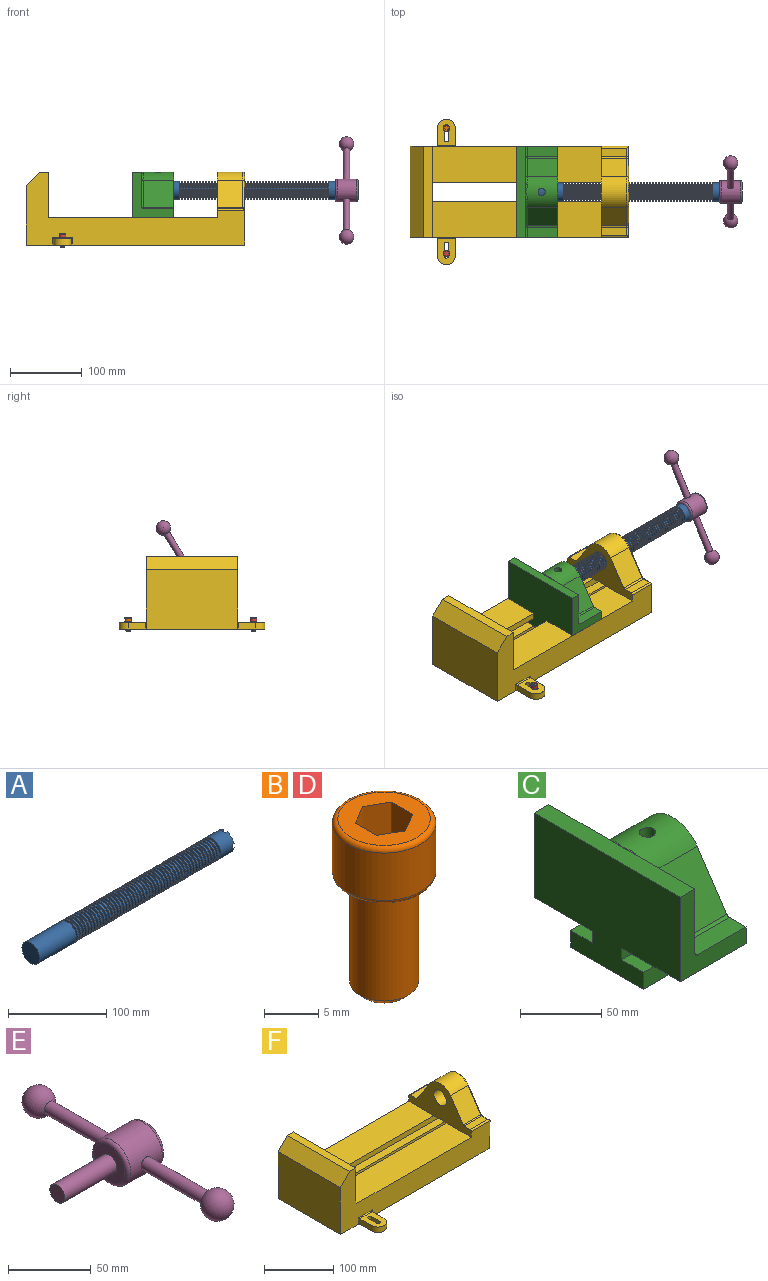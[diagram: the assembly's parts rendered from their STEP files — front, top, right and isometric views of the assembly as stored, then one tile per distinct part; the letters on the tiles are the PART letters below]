
ASSEMBLY  parts=6 mates=6
PART A: 220 faces, bbox 279.4x25.4x25.4 mm
  f0: cylinder r=12.7mm len=25.4mm, axis (-1,0,0), area 1468.2mm2, adj f1,f2,f3,f5,f7,f208,f209,f210
  f1: plane 9.9x9.9mm, normal (1,0,0), area 62.3mm2, adj f0,f4,f213,f216
  f2: plane 9.9x9.9mm, normal (1,0,0), area 62.3mm2, adj f0,f4,f210,f218
  f3: plane 9.9x9.9mm, normal (1,0,0), area 62.3mm2, adj f0,f4,f209,f212
  f4: cylinder r=6.35mm len=25.4mm, axis (1,0,0), area 960.3mm2, adj f1,f2,f3,f5,f6,f208,f209,f210
  f5: plane 9.9x9.9mm, normal (1,0,0), area 62.3mm2, adj f0,f4,f215,f217
  f6: plane 12.7x12.7mm, normal (1,0,0), area 126.7mm2, adj f4
  f7: cone r=12.7mm half-angle=76deg, axis (1,0,0), area 188mm2, adj f0,f9
  f8: cone r=10.16mm half-angle=76deg, axis (-1,0,0), area 188mm2, adj f9,f10
  f9: cylinder r=10.16mm len=20.32mm, axis (1,0,0), area 81.1mm2, adj f7,f8
  f10: cylinder r=12.7mm len=25.4mm, axis (-1,0,0), area 131.7mm2, adj f8,f11
  f11: cone r=12.7mm half-angle=76deg, axis (1,0,0), area 188mm2, adj f10,f13
  f12: cone r=10.16mm half-angle=76deg, axis (-1,0,0), area 188mm2, adj f13,f14
  f13: cylinder r=10.16mm len=20.32mm, axis (1,0,0), area 81.1mm2, adj f11,f12
  f14: cylinder r=12.7mm len=25.4mm, axis (-1,0,0), area 131.7mm2, adj f12,f15
  f15: cone r=12.7mm half-angle=76deg, axis (1,0,0), area 188mm2, adj f14,f17
  f16: cone r=10.16mm half-angle=76deg, axis (-1,0,0), area 188mm2, adj f17,f18
  f17: cylinder r=10.16mm len=20.32mm, axis (1,0,0), area 81.1mm2, adj f15,f16
  f18: cylinder r=12.7mm len=25.4mm, axis (-1,0,0), area 131.7mm2, adj f16,f19
  f19: cone r=12.7mm half-angle=76deg, axis (1,0,0), area 188mm2, adj f18,f21
  f20: cone r=10.16mm half-angle=76deg, axis (-1,0,0), area 188mm2, adj f21,f22
  f21: cylinder r=10.16mm len=20.32mm, axis (1,0,0), area 81.1mm2, adj f19,f20
  f22: cylinder r=12.7mm len=25.4mm, axis (-1,0,0), area 131.7mm2, adj f20,f23
  f23: cone r=12.7mm half-angle=76deg, axis (1,0,0), area 188mm2, adj f22,f25
  f24: cone r=10.16mm half-angle=76deg, axis (-1,0,0), area 188mm2, adj f25,f26
  f25: cylinder r=10.16mm len=20.32mm, axis (1,0,0), area 81.1mm2, adj f23,f24
  f26: cylinder r=12.7mm len=25.4mm, axis (-1,0,0), area 131.7mm2, adj f24,f27
  f27: cone r=12.7mm half-angle=76deg, axis (1,0,0), area 188mm2, adj f26,f29
  f28: cone r=10.16mm half-angle=76deg, axis (-1,0,0), area 188mm2, adj f29,f30
  f29: cylinder r=10.16mm len=20.32mm, axis (1,0,0), area 81.1mm2, adj f27,f28
  f30: cylinder r=12.7mm len=25.4mm, axis (-1,0,0), area 131.7mm2, adj f28,f31
  f31: cone r=12.7mm half-angle=76deg, axis (1,0,0), area 188mm2, adj f30,f33
  f32: cone r=10.16mm half-angle=76deg, axis (-1,0,0), area 188mm2, adj f33,f34
  f33: cylinder r=10.16mm len=20.32mm, axis (1,0,0), area 81.1mm2, adj f31,f32
  f34: cylinder r=12.7mm len=25.4mm, axis (-1,0,0), area 131.7mm2, adj f32,f35
  f35: cone r=12.7mm half-angle=76deg, axis (1,0,0), area 188mm2, adj f34,f37
  f36: cone r=10.16mm half-angle=76deg, axis (-1,0,0), area 188mm2, adj f37,f38
  f37: cylinder r=10.16mm len=20.32mm, axis (1,0,0), area 81.1mm2, adj f35,f36
  f38: cylinder r=12.7mm len=25.4mm, axis (-1,0,0), area 131.7mm2, adj f36,f39
  f39: cone r=12.7mm half-angle=76deg, axis (1,0,0), area 188mm2, adj f38,f41
  f40: cone r=10.16mm half-angle=76deg, axis (-1,0,0), area 188mm2, adj f41,f42
  f41: cylinder r=10.16mm len=20.32mm, axis (1,0,0), area 81.1mm2, adj f39,f40
  f42: cylinder r=12.7mm len=25.4mm, axis (-1,0,0), area 131.7mm2, adj f40,f43
  f43: cone r=12.7mm half-angle=76deg, axis (1,0,0), area 188mm2, adj f42,f45
  f44: cone r=10.16mm half-angle=76deg, axis (-1,0,0), area 188mm2, adj f45,f46
  f45: cylinder r=10.16mm len=20.32mm, axis (1,0,0), area 81.1mm2, adj f43,f44
  f46: cylinder r=12.7mm len=25.4mm, axis (-1,0,0), area 131.7mm2, adj f44,f47
  f47: cone r=12.7mm half-angle=76deg, axis (1,0,0), area 188mm2, adj f46,f49
  f48: cone r=10.16mm half-angle=76deg, axis (-1,0,0), area 188mm2, adj f49,f50
  f49: cylinder r=10.16mm len=20.32mm, axis (1,0,0), area 81.1mm2, adj f47,f48
  f50: cylinder r=12.7mm len=25.4mm, axis (-1,0,0), area 131.7mm2, adj f48,f51
  f51: cone r=12.7mm half-angle=76deg, axis (1,0,0), area 188mm2, adj f50,f53
  f52: cone r=10.16mm half-angle=76deg, axis (-1,0,0), area 188mm2, adj f53,f54
  f53: cylinder r=10.16mm len=20.32mm, axis (1,0,0), area 81.1mm2, adj f51,f52
  f54: cylinder r=12.7mm len=25.4mm, axis (-1,0,0), area 131.7mm2, adj f52,f55
  f55: cone r=12.7mm half-angle=76deg, axis (1,0,0), area 188mm2, adj f54,f57
  f56: cone r=10.16mm half-angle=76deg, axis (-1,0,0), area 188mm2, adj f57,f58
  f57: cylinder r=10.16mm len=20.32mm, axis (1,0,0), area 81.1mm2, adj f55,f56
  f58: cylinder r=12.7mm len=25.4mm, axis (-1,0,0), area 131.7mm2, adj f56,f59
  f59: cone r=12.7mm half-angle=76deg, axis (1,0,0), area 188mm2, adj f58,f61
  f60: cone r=10.16mm half-angle=76deg, axis (-1,0,0), area 188mm2, adj f61,f62
  f61: cylinder r=10.16mm len=20.32mm, axis (1,0,0), area 81.1mm2, adj f59,f60
  f62: cylinder r=12.7mm len=25.4mm, axis (-1,0,0), area 131.7mm2, adj f60,f63
  f63: cone r=12.7mm half-angle=76deg, axis (1,0,0), area 188mm2, adj f62,f65
  f64: cone r=10.16mm half-angle=76deg, axis (-1,0,0), area 188mm2, adj f65,f66
  f65: cylinder r=10.16mm len=20.32mm, axis (1,0,0), area 81.1mm2, adj f63,f64
  f66: cylinder r=12.7mm len=25.4mm, axis (-1,0,0), area 131.7mm2, adj f64,f67
  f67: cone r=12.7mm half-angle=76deg, axis (1,0,0), area 188mm2, adj f66,f69
  f68: cone r=10.16mm half-angle=76deg, axis (-1,0,0), area 188mm2, adj f69,f70
  f69: cylinder r=10.16mm len=20.32mm, axis (1,0,0), area 81.1mm2, adj f67,f68
  f70: cylinder r=12.7mm len=25.4mm, axis (-1,0,0), area 131.7mm2, adj f68,f71
  f71: cone r=12.7mm half-angle=76deg, axis (1,0,0), area 188mm2, adj f70,f73
  f72: cone r=10.16mm half-angle=76deg, axis (-1,0,0), area 188mm2, adj f73,f74
  f73: cylinder r=10.16mm len=20.32mm, axis (1,0,0), area 81.1mm2, adj f71,f72
  f74: cylinder r=12.7mm len=25.4mm, axis (-1,0,0), area 131.7mm2, adj f72,f75
  f75: cone r=12.7mm half-angle=76deg, axis (1,0,0), area 188mm2, adj f74,f77
  f76: cone r=10.16mm half-angle=76deg, axis (-1,0,0), area 188mm2, adj f77,f78
  f77: cylinder r=10.16mm len=20.32mm, axis (1,0,0), area 81.1mm2, adj f75,f76
  f78: cylinder r=12.7mm len=25.4mm, axis (-1,0,0), area 131.7mm2, adj f76,f79
  f79: cone r=12.7mm half-angle=76deg, axis (1,0,0), area 188mm2, adj f78,f81
  f80: cone r=10.16mm half-angle=76deg, axis (-1,0,0), area 188mm2, adj f81,f82
  f81: cylinder r=10.16mm len=20.32mm, axis (1,0,0), area 81.1mm2, adj f79,f80
  f82: cylinder r=12.7mm len=25.4mm, axis (-1,0,0), area 131.7mm2, adj f80,f83
  f83: cone r=12.7mm half-angle=76deg, axis (1,0,0), area 188mm2, adj f82,f85
  f84: cone r=10.16mm half-angle=76deg, axis (-1,0,0), area 188mm2, adj f85,f86
  f85: cylinder r=10.16mm len=20.32mm, axis (1,0,0), area 81.1mm2, adj f83,f84
  f86: cylinder r=12.7mm len=25.4mm, axis (-1,0,0), area 131.7mm2, adj f84,f87
  f87: cone r=12.7mm half-angle=76deg, axis (1,0,0), area 188mm2, adj f86,f89
  f88: cone r=10.16mm half-angle=76deg, axis (-1,0,0), area 188mm2, adj f89,f90
  f89: cylinder r=10.16mm len=20.32mm, axis (1,0,0), area 81.1mm2, adj f87,f88
  f90: cylinder r=12.7mm len=25.4mm, axis (-1,0,0), area 131.7mm2, adj f88,f91
  f91: cone r=12.7mm half-angle=76deg, axis (1,0,0), area 188mm2, adj f90,f93
  f92: cone r=10.16mm half-angle=76deg, axis (-1,0,0), area 188mm2, adj f93,f94
  f93: cylinder r=10.16mm len=20.32mm, axis (1,0,0), area 81.1mm2, adj f91,f92
  f94: cylinder r=12.7mm len=25.4mm, axis (-1,0,0), area 131.7mm2, adj f92,f95
  f95: cone r=12.7mm half-angle=76deg, axis (1,0,0), area 188mm2, adj f94,f97
  f96: cone r=10.16mm half-angle=76deg, axis (-1,0,0), area 188mm2, adj f97,f98
  f97: cylinder r=10.16mm len=20.32mm, axis (1,0,0), area 81.1mm2, adj f95,f96
  f98: cylinder r=12.7mm len=25.4mm, axis (-1,0,0), area 131.7mm2, adj f96,f99
  f99: cone r=12.7mm half-angle=76deg, axis (1,0,0), area 188mm2, adj f98,f101
  f100: cone r=10.16mm half-angle=76deg, axis (-1,0,0), area 188mm2, adj f101,f102
  f101: cylinder r=10.16mm len=20.32mm, axis (1,0,0), area 81.1mm2, adj f99,f100
  f102: cylinder r=12.7mm len=25.4mm, axis (-1,0,0), area 131.7mm2, adj f100,f103
  f103: cone r=12.7mm half-angle=76deg, axis (1,0,0), area 188mm2, adj f102,f105
  f104: cone r=10.16mm half-angle=76deg, axis (-1,0,0), area 188mm2, adj f105,f106
  f105: cylinder r=10.16mm len=20.32mm, axis (1,0,0), area 81.1mm2, adj f103,f104
  f106: cylinder r=12.7mm len=25.4mm, axis (-1,0,0), area 131.7mm2, adj f104,f107
  f107: cone r=12.7mm half-angle=76deg, axis (1,0,0), area 188mm2, adj f106,f109
  f108: cone r=10.16mm half-angle=76deg, axis (-1,0,0), area 188mm2, adj f109,f110
  f109: cylinder r=10.16mm len=20.32mm, axis (1,0,0), area 81.1mm2, adj f107,f108
  f110: cylinder r=12.7mm len=25.4mm, axis (-1,0,0), area 131.7mm2, adj f108,f111
  f111: cone r=12.7mm half-angle=76deg, axis (1,0,0), area 188mm2, adj f110,f113
  f112: cone r=10.16mm half-angle=76deg, axis (-1,0,0), area 188mm2, adj f113,f114
  f113: cylinder r=10.16mm len=20.32mm, axis (1,0,0), area 81.1mm2, adj f111,f112
  f114: cylinder r=12.7mm len=25.4mm, axis (-1,0,0), area 131.7mm2, adj f112,f115
  f115: cone r=12.7mm half-angle=76deg, axis (1,0,0), area 188mm2, adj f114,f117
  f116: cone r=10.16mm half-angle=76deg, axis (-1,0,0), area 188mm2, adj f117,f118
  f117: cylinder r=10.16mm len=20.32mm, axis (1,0,0), area 81.1mm2, adj f115,f116
  f118: cylinder r=12.7mm len=25.4mm, axis (-1,0,0), area 131.7mm2, adj f116,f119
  f119: cone r=12.7mm half-angle=76deg, axis (1,0,0), area 188mm2, adj f118,f121
  f120: cone r=10.16mm half-angle=76deg, axis (-1,0,0), area 188mm2, adj f121,f122
  f121: cylinder r=10.16mm len=20.32mm, axis (1,0,0), area 81.1mm2, adj f119,f120
  f122: cylinder r=12.7mm len=25.4mm, axis (-1,0,0), area 131.7mm2, adj f120,f123
  f123: cone r=12.7mm half-angle=76deg, axis (1,0,0), area 188mm2, adj f122,f125
  f124: cone r=10.16mm half-angle=76deg, axis (-1,0,0), area 188mm2, adj f125,f126
  f125: cylinder r=10.16mm len=20.32mm, axis (1,0,0), area 81.1mm2, adj f123,f124
  f126: cylinder r=12.7mm len=25.4mm, axis (-1,0,0), area 131.7mm2, adj f124,f127
  f127: cone r=12.7mm half-angle=76deg, axis (1,0,0), area 188mm2, adj f126,f129
  f128: cone r=10.16mm half-angle=76deg, axis (-1,0,0), area 188mm2, adj f129,f130
  f129: cylinder r=10.16mm len=20.32mm, axis (1,0,0), area 81.1mm2, adj f127,f128
  f130: cylinder r=12.7mm len=25.4mm, axis (-1,0,0), area 131.7mm2, adj f128,f131
  f131: cone r=12.7mm half-angle=76deg, axis (1,0,0), area 188mm2, adj f130,f133
  f132: cone r=10.16mm half-angle=76deg, axis (-1,0,0), area 188mm2, adj f133,f134
  f133: cylinder r=10.16mm len=20.32mm, axis (1,0,0), area 81.1mm2, adj f131,f132
  f134: cylinder r=12.7mm len=25.4mm, axis (-1,0,0), area 131.7mm2, adj f132,f135
  f135: cone r=12.7mm half-angle=76deg, axis (1,0,0), area 188mm2, adj f134,f137
  f136: cone r=10.16mm half-angle=76deg, axis (-1,0,0), area 188mm2, adj f137,f138
  f137: cylinder r=10.16mm len=20.32mm, axis (1,0,0), area 81.1mm2, adj f135,f136
  f138: cylinder r=12.7mm len=25.4mm, axis (-1,0,0), area 131.7mm2, adj f136,f139
  f139: cone r=12.7mm half-angle=76deg, axis (1,0,0), area 188mm2, adj f138,f141
  f140: cone r=10.16mm half-angle=76deg, axis (-1,0,0), area 188mm2, adj f141,f142
  f141: cylinder r=10.16mm len=20.32mm, axis (1,0,0), area 81.1mm2, adj f139,f140
  f142: cylinder r=12.7mm len=25.4mm, axis (-1,0,0), area 131.7mm2, adj f140,f143
  f143: cone r=12.7mm half-angle=76deg, axis (1,0,0), area 188mm2, adj f142,f145
  f144: cone r=10.16mm half-angle=76deg, axis (-1,0,0), area 188mm2, adj f145,f146
  f145: cylinder r=10.16mm len=20.32mm, axis (1,0,0), area 81.1mm2, adj f143,f144
  f146: cylinder r=12.7mm len=25.4mm, axis (-1,0,0), area 131.7mm2, adj f144,f147
  f147: cone r=12.7mm half-angle=76deg, axis (1,0,0), area 188mm2, adj f146,f149
  f148: cone r=10.16mm half-angle=76deg, axis (-1,0,0), area 188mm2, adj f149,f150
  f149: cylinder r=10.16mm len=20.32mm, axis (1,0,0), area 81.1mm2, adj f147,f148
  f150: cylinder r=12.7mm len=25.4mm, axis (-1,0,0), area 131.7mm2, adj f148,f151
  f151: cone r=12.7mm half-angle=76deg, axis (1,0,0), area 188mm2, adj f150,f153
  f152: cone r=10.16mm half-angle=76deg, axis (-1,0,0), area 188mm2, adj f153,f154
  f153: cylinder r=10.16mm len=20.32mm, axis (1,0,0), area 81.1mm2, adj f151,f152
  f154: cylinder r=12.7mm len=25.4mm, axis (-1,0,0), area 131.7mm2, adj f152,f155
  f155: cone r=12.7mm half-angle=76deg, axis (1,0,0), area 188mm2, adj f154,f157
  f156: cone r=10.16mm half-angle=76deg, axis (-1,0,0), area 188mm2, adj f157,f158
  f157: cylinder r=10.16mm len=20.32mm, axis (1,0,0), area 81.1mm2, adj f155,f156
  f158: cylinder r=12.7mm len=25.4mm, axis (-1,0,0), area 131.7mm2, adj f156,f159
  f159: cone r=12.7mm half-angle=76deg, axis (1,0,0), area 188mm2, adj f158,f161
  f160: cone r=10.16mm half-angle=76deg, axis (-1,0,0), area 188mm2, adj f161,f162
  f161: cylinder r=10.16mm len=20.32mm, axis (1,0,0), area 81.1mm2, adj f159,f160
  f162: cylinder r=12.7mm len=25.4mm, axis (-1,0,0), area 131.7mm2, adj f160,f163
  f163: cone r=12.7mm half-angle=76deg, axis (1,0,0), area 188mm2, adj f162,f165
  f164: cone r=10.16mm half-angle=76deg, axis (-1,0,0), area 188mm2, adj f165,f166
  f165: cylinder r=10.16mm len=20.32mm, axis (1,0,0), area 81.1mm2, adj f163,f164
  f166: cylinder r=12.7mm len=25.4mm, axis (-1,0,0), area 131.7mm2, adj f164,f167
  f167: cone r=12.7mm half-angle=76deg, axis (1,0,0), area 188mm2, adj f166,f169
  f168: cone r=10.16mm half-angle=76deg, axis (-1,0,0), area 188mm2, adj f169,f170
  f169: cylinder r=10.16mm len=20.32mm, axis (1,0,0), area 81.1mm2, adj f167,f168
  f170: cylinder r=12.7mm len=25.4mm, axis (-1,0,0), area 131.7mm2, adj f168,f171
  f171: cone r=12.7mm half-angle=76deg, axis (1,0,0), area 188mm2, adj f170,f173
  f172: cone r=10.16mm half-angle=76deg, axis (-1,0,0), area 188mm2, adj f173,f174
  f173: cylinder r=10.16mm len=20.32mm, axis (1,0,0), area 81.1mm2, adj f171,f172
  f174: cylinder r=12.7mm len=25.4mm, axis (-1,0,0), area 131.7mm2, adj f172,f175
  f175: cone r=12.7mm half-angle=76deg, axis (1,0,0), area 188mm2, adj f174,f177
  f176: cone r=10.16mm half-angle=76deg, axis (-1,0,0), area 188mm2, adj f177,f178
  f177: cylinder r=10.16mm len=20.32mm, axis (1,0,0), area 81.1mm2, adj f175,f176
  f178: cylinder r=12.7mm len=25.4mm, axis (-1,0,0), area 131.7mm2, adj f176,f179
  f179: cone r=12.7mm half-angle=76deg, axis (1,0,0), area 188mm2, adj f178,f181
  f180: cone r=10.16mm half-angle=76deg, axis (-1,0,0), area 188mm2, adj f181,f182
  f181: cylinder r=10.16mm len=20.32mm, axis (1,0,0), area 81.1mm2, adj f179,f180
  f182: cylinder r=12.7mm len=25.4mm, axis (-1,0,0), area 131.7mm2, adj f180,f183
  f183: cone r=12.7mm half-angle=76deg, axis (1,0,0), area 188mm2, adj f182,f185
  f184: cone r=10.16mm half-angle=76deg, axis (-1,0,0), area 188mm2, adj f185,f186
  f185: cylinder r=10.16mm len=20.32mm, axis (1,0,0), area 81.1mm2, adj f183,f184
  f186: cylinder r=12.7mm len=25.4mm, axis (-1,0,0), area 131.7mm2, adj f184,f187
  f187: cone r=12.7mm half-angle=76deg, axis (1,0,0), area 188mm2, adj f186,f189
  f188: cone r=10.16mm half-angle=76deg, axis (-1,0,0), area 188mm2, adj f189,f190
  f189: cylinder r=10.16mm len=20.32mm, axis (1,0,0), area 81.1mm2, adj f187,f188
  f190: cylinder r=12.7mm len=25.4mm, axis (-1,0,0), area 131.7mm2, adj f188,f191
  f191: cone r=12.7mm half-angle=76deg, axis (1,0,0), area 188mm2, adj f190,f193
  f192: cone r=10.16mm half-angle=76deg, axis (-1,0,0), area 188mm2, adj f193,f194
  f193: cylinder r=10.16mm len=20.32mm, axis (1,0,0), area 81.1mm2, adj f191,f192
  f194: cylinder r=12.7mm len=25.4mm, axis (-1,0,0), area 131.7mm2, adj f192,f195
  f195: cone r=12.7mm half-angle=76deg, axis (1,0,0), area 188mm2, adj f194,f197
  f196: cone r=10.16mm half-angle=76deg, axis (-1,0,0), area 188mm2, adj f197,f198
  f197: cylinder r=10.16mm len=20.32mm, axis (1,0,0), area 81.1mm2, adj f195,f196
  f198: cylinder r=12.7mm len=25.4mm, axis (-1,0,0), area 131.7mm2, adj f196,f199
  f199: cone r=12.7mm half-angle=76deg, axis (1,0,0), area 188mm2, adj f198,f201
  f200: cone r=10.16mm half-angle=76deg, axis (-1,0,0), area 188mm2, adj f201,f202
  f201: cylinder r=10.16mm len=20.32mm, axis (1,0,0), area 81.1mm2, adj f199,f200
  f202: cylinder r=12.7mm len=25.4mm, axis (-1,0,0), area 131.7mm2, adj f200,f203
  f203: cone r=12.7mm half-angle=76deg, axis (1,0,0), area 188mm2, adj f202,f205
  f204: cone r=10.16mm half-angle=76deg, axis (-1,0,0), area 188mm2, adj f205,f207
  f205: cylinder r=10.16mm len=20.32mm, axis (1,0,0), area 81.1mm2, adj f203,f204
  f206: plane 25.4x25.4mm, normal (-1,0,0), area 506.7mm2, adj f207
  f207: cylinder r=12.7mm len=52.45mm, axis (-1,0,0), area 4185.4mm2, adj f204,f206
  f208: plane 6.88x5.08mm, normal (1,0,0), area 32.7mm2, adj f0,f4,f209,f210
  f209: plane 6.62x2.54mm, normal (0,-1,0), area 16.8mm2, adj f0,f3,f4,f208
  f210: plane 6.62x2.54mm, normal (0,1,0), area 16.8mm2, adj f0,f2,f4,f208
  f211: plane 6.88x5.08mm, normal (1,0,0), area 32.7mm2, adj f0,f4,f212,f213
  f212: plane 6.62x2.54mm, normal (0,0,1), area 16.8mm2, adj f0,f3,f4,f211
  f213: plane 6.62x2.54mm, normal (0,0,-1), area 16.8mm2, adj f0,f1,f4,f211
  f214: plane 6.88x5.08mm, normal (1,0,0), area 32.7mm2, adj f0,f4,f215,f216
  f215: plane 6.62x2.54mm, normal (0,1,0), area 16.8mm2, adj f0,f4,f5,f214
  f216: plane 6.62x2.54mm, normal (0,-1,0), area 16.8mm2, adj f0,f1,f4,f214
  f217: plane 6.62x2.54mm, normal (0,0,-1), area 16.8mm2, adj f0,f4,f5,f219
  f218: plane 6.62x2.54mm, normal (0,0,1), area 16.8mm2, adj f0,f2,f4,f219
  f219: plane 6.88x5.08mm, normal (1,0,0), area 32.7mm2, adj f0,f4,f217,f218
PART B: 15 faces, bbox 10.3x10.3x19.1 mm
  f0: plane 8.51x8.51mm, normal (0,0,1), area 37.2mm2, adj f5,f6,f7,f8,f9,f10,f14
  f1: cylinder r=3.17mm len=11.94mm, axis (0,0,1), area 238.2mm2, adj f4,f12
  f2: plane 4.83x4.83mm, normal (0,0,-1), area 18.3mm2, adj f12
  f3: cylinder r=4.76mm len=9.53mm, axis (0,0,-1), area 159.6mm2, adj f13,f14
  f4: plane 8.51x8.51mm, normal (0,0,-1), area 25.2mm2, adj f1,f13
  f5: plane 4.83x2.38mm, normal (-0.5,-0.87,0), area 13.3mm2, adj f0,f6,f10,f11
  f6: plane 4.83x2.38mm, normal (0.5,-0.87,0), area 13.3mm2, adj f0,f5,f7,f11
  f7: plane 4.83x2.75mm, normal (1,0,0), area 13.3mm2, adj f0,f6,f8,f11
  f8: plane 4.83x2.38mm, normal (0.5,0.87,0), area 13.3mm2, adj f0,f7,f9,f11
  f9: plane 4.83x2.38mm, normal (-0.5,0.87,0), area 13.3mm2, adj f0,f8,f10,f11
  f10: plane 4.83x2.75mm, normal (-1,0,0), area 13.3mm2, adj f0,f5,f9,f11
  f11: plane 5.5x4.76mm, normal (0,0,1), area 19.6mm2, adj f5,f6,f7,f8,f9,f10
  f12: cone r=3.17mm half-angle=45deg, axis (0,0,1), area 18.9mm2, adj f1,f2
  f13: torus R=4.25mm, axis (0,0,1), area 23mm2, adj f3,f4
  f14: torus R=4.25mm, axis (0,0,1), area 23mm2, adj f0,f3
PART C: 36 faces, bbox 57.2x127x89 mm
  f0: plane 57.15x50.8mm, normal (0,0,-1), area 2903.2mm2, adj f6,f9,f10,f23
  f1: cylinder r=12.7mm len=44.45mm, axis (1,0,0), area 3464.3mm2, adj f6,f15,f16
  f2: plane 41.91x14.52mm, normal (0,0,1), area 608.5mm2, adj f6,f11,f24,f25
  f3: plane 51.86x48.26mm, normal (1,0,0), area 1495.7mm2, adj f8,f10,f31,f33,f35
  f4: plane 51.86x48.26mm, normal (1,0,0), area 1495.7mm2, adj f8,f11,f24,f28,f29
  f5: plane 57.15x50.8mm, normal (0,0,-1), area 2903.2mm2, adj f6,f9,f11,f22
  f6: plane 127x85.09mm, normal (1,0,0), area 5190.6mm2, adj f0,f1,f2,f5,f7,f10,f11,f12
  f7: plane 41.91x14.52mm, normal (0,0,1), area 608.5mm2, adj f6,f10,f30,f31
  f8: plane 127x12.7mm, normal (0,0,1), area 1612.9mm2, adj f3,f4,f9,f10,f11,f26,f34
  f9: plane 127x85.09mm, normal (-1,0,0), area 9096.8mm2, adj f0,f5,f8,f10,f11,f17,f18,f19
  f10: plane 63.5x57.15mm, normal (0,-1,0), area 1372.3mm2, adj f0,f3,f6,f7,f8,f9,f31
  f11: plane 63.5x57.15mm, normal (0,1,0), area 1372.3mm2, adj f2,f4,f5,f6,f8,f9,f24
  f12: plane 41.91x38.43mm, normal (0,-0.83,0.56), area 1939.2mm2, adj f6,f13,f30,f33
  f13: cylinder r=25.4mm len=44.45mm, axis (1,0,0), area 2026.5mm2, adj f6,f12,f14,f16,f26,f28,f34,f35
  f14: plane 41.91x38.43mm, normal (0,0.83,0.56), area 1939.2mm2, adj f6,f13,f25,f29
  f15: plane 25.4x25.4mm, normal (1,0,0), area 506.7mm2, adj f1
  f16: cylinder r=5.08mm len=13.76mm, axis (0,0,1), area 414mm2, adj f1,f13
  f17: plane 57.15x19.05mm, normal (0,0,1), area 1088.7mm2, adj f6,f9,f18,f23
  f18: plane 57.15x12.7mm, normal (0,-1,0), area 725.8mm2, adj f6,f9,f17,f19
  f19: plane 63.5x57.15mm, normal (0,0,-1), area 3629mm2, adj f6,f9,f18,f20
  f20: plane 57.15x12.7mm, normal (0,1,0), area 725.8mm2, adj f6,f9,f19,f21
  f21: plane 57.15x19.05mm, normal (0,0,1), area 1088.7mm2, adj f6,f9,f20,f22
  f22: plane 57.15x8.89mm, normal (0,1,0), area 508.1mm2, adj f5,f6,f9,f21
  f23: plane 57.15x8.89mm, normal (0,-1,0), area 508.1mm2, adj f0,f6,f9,f17
  f24: cylinder r=2.54mm len=14.52mm, axis (0,-1,0), area 57.9mm2, adj f2,f4,f11,f27
  f25: cylinder r=2.54mm len=41.91mm, axis (1,0,0), area 104.3mm2, adj f2,f6,f14,f27
  f26: bspline ~12.24x2.8mm, area 20.9mm2, adj f8,f13,f28
  f27: sphere r=2.54mm, area 6.3mm2, adj f24,f25,f29
  f28: torus R=27.94mm, axis (1,0,0), area 57.8mm2, adj f4,f13,f26,f29
  f29: cylinder r=2.54mm len=39.84mm, axis (0,-0.56,0.83), area 184.6mm2, adj f4,f14,f27,f28
  f30: cylinder r=2.54mm len=41.91mm, axis (1,0,0), area 104.3mm2, adj f6,f7,f12,f32
  f31: cylinder r=2.54mm len=14.52mm, axis (0,-1,0), area 57.9mm2, adj f3,f7,f10,f32
  f32: sphere r=2.54mm, area 6.3mm2, adj f30,f31,f33
  f33: cylinder r=2.54mm len=39.84mm, axis (0,-0.56,-0.83), area 184.6mm2, adj f3,f12,f32,f35
  f34: bspline ~12.24x2.8mm, area 20.9mm2, adj f8,f13,f35
  f35: torus R=27.94mm, axis (1,0,0), area 57.8mm2, adj f3,f13,f33,f34
PART D: same geometry as B
PART E: 11 faces, bbox 76.2x172.7x34.4 mm
  f0: sphere r=10.16mm, area 1231.8mm2, adj f1
  f1: cylinder r=4.45mm len=51.82mm, axis (0,1,0), area 1438.5mm2, adj f0,f4
  f2: sphere r=10.16mm, area 1231.8mm2, adj f3
  f3: cylinder r=4.45mm len=51.82mm, axis (0,1,0), area 1438.5mm2, adj f2,f4
  f4: cylinder r=15.88mm len=31.75mm, axis (-1,0,0), area 2534.7mm2, adj f1,f3,f9,f10
  f5: cylinder r=6.35mm len=44.45mm, axis (-1,0,0), area 1773.5mm2, adj f6,f8
  f6: plane 12.7x12.7mm, normal (-1,0,0), area 126.7mm2, adj f5
  f7: plane 26.67x26.67mm, normal (1,0,0), area 558.6mm2, adj f10
  f8: plane 26.67x26.67mm, normal (-1,0,0), area 432mm2, adj f5,f9
  f9: torus R=13.33mm, axis (1,0,0), area 374.8mm2, adj f4,f8
  f10: torus R=13.33mm, axis (1,0,0), area 374.8mm2, adj f4,f7
PART F: 61 faces, bbox 304.8x203.2x103.7 mm
  f0: plane 304.8x101.6mm, normal (0,1,0), area 13520.3mm2, adj f3,f4,f5,f6,f7,f8,f9,f16
  f1: plane 304.8x101.6mm, normal (0,-1,0), area 13520.3mm2, adj f2,f3,f5,f6,f7,f8,f9,f16
  f2: plane 234.95x50.8mm, normal (0,0,1), area 11935.5mm2, adj f1,f5,f16,f26
  f3: plane 127x99.06mm, normal (1,0,0), area 7097.5mm2, adj f0,f1,f9,f14,f17,f18,f19,f20
  f4: plane 234.95x50.8mm, normal (0,0,1), area 11935.5mm2, adj f0,f5,f16,f27
  f5: plane 127x101.6mm, normal (1,0,0), area 9516.1mm2, adj f0,f1,f2,f4,f6,f9,f18,f19
  f6: plane 127x12.7mm, normal (0,0,1), area 1612.9mm2, adj f0,f1,f5,f7
  f7: plane 127x19.05mm, normal (-0.71,0,0.71), area 3421.5mm2, adj f0,f1,f6,f8
  f8: plane 127x82.55mm, normal (-1,0,0), area 10483.8mm2, adj f0,f1,f7,f9
  f9: plane 304.8x203.2mm, normal (0,0,-1), area 33298.3mm2, adj f0,f1,f3,f5,f8,f21,f22,f39
  f10: plane 35.56x11.98mm, normal (0,0,1), area 426mm2, adj f16,f28,f29,f30
  f11: plane 38.43x35.56mm, normal (0,0.83,0.56), area 1645.4mm2, adj f12,f16,f29,f32
  f12: cylinder r=25.4mm len=42.19mm, axis (1,0,0), area 1770.2mm2, adj f11,f13,f16,f33
  f13: plane 38.43x35.56mm, normal (0,-0.83,0.56), area 1645.4mm2, adj f12,f16,f34,f35
  f14: cylinder r=12.7mm len=38.1mm, axis (1,0,0), area 3040.2mm2, adj f3,f16
  f15: plane 35.56x11.98mm, normal (0,0,1), area 426mm2, adj f16,f34,f36,f38
  f16: plane 127x63.5mm, normal (-1,0,0), area 4155.5mm2, adj f0,f1,f2,f4,f10,f11,f12,f13
  f17: plane 38.1x25.4mm, normal (0,0,-1), area 967.7mm2, adj f3,f16,f26,f27
  f18: plane 273.05x19.05mm, normal (0,0,-1), area 5201.6mm2, adj f3,f5,f19,f26
  f19: plane 273.05x12.7mm, normal (0,1,0), area 3467.7mm2, adj f3,f5,f18,f20
  f20: plane 273.05x19.05mm, normal (0,0,1), area 5201.6mm2, adj f3,f5,f19,f21
  f21: plane 273.05x16.51mm, normal (0,1,0), area 4508.1mm2, adj f3,f5,f9,f20
  f22: plane 273.05x16.51mm, normal (0,-1,0), area 4508.1mm2, adj f3,f5,f9,f23
  f23: plane 273.05x19.05mm, normal (0,0,1), area 5201.6mm2, adj f3,f5,f22,f24
  f24: plane 273.05x12.7mm, normal (0,-1,0), area 3467.7mm2, adj f3,f5,f23,f25
  f25: plane 273.05x19.05mm, normal (0,0,-1), area 5201.6mm2, adj f3,f5,f24,f27
  f26: plane 273.05x8.89mm, normal (0,1,0), area 2427.4mm2, adj f2,f3,f5,f17,f18
  f27: plane 273.05x8.89mm, normal (0,-1,0), area 2427.4mm2, adj f3,f4,f5,f17,f25
  f28: cylinder r=2.54mm len=38.1mm, axis (1,0,0), area 148.3mm2, adj f0,f10,f16,f30
  f29: cylinder r=2.54mm len=35.56mm, axis (-1,0,0), area 88.5mm2, adj f10,f11,f16,f31
  f30: cylinder r=2.54mm len=14.52mm, axis (0,1,0), area 54.3mm2, adj f3,f10,f28,f31
  f31: torus R=5.08mm, axis (-1,0,0), area 13.5mm2, adj f3,f29,f30,f32
  f32: cylinder r=2.54mm len=39.84mm, axis (0,0.56,-0.83), area 184.6mm2, adj f3,f11,f31,f33
  f33: torus R=22.86mm, axis (-1,0,0), area 191.4mm2, adj f3,f12,f32,f35
  f34: cylinder r=2.54mm len=35.56mm, axis (-1,0,0), area 88.5mm2, adj f13,f15,f16,f37
  f35: cylinder r=2.54mm len=39.84mm, axis (0,0.56,0.83), area 184.6mm2, adj f3,f13,f33,f37
  f36: cylinder r=2.54mm len=38.1mm, axis (-1,0,0), area 148.3mm2, adj f1,f15,f16,f38
  f37: torus R=5.08mm, axis (-1,0,0), area 13.5mm2, adj f3,f34,f35,f38
  f38: cylinder r=2.54mm len=14.52mm, axis (0,1,0), area 54.3mm2, adj f3,f15,f36,f37
  f39: plane 23.88x9.53mm, normal (-1,0,0), area 227.4mm2, adj f9,f45,f46,f60
  f40: plane 23.88x9.53mm, normal (1,0,0), area 227.4mm2, adj f9,f45,f46,f58
  f41: cylinder r=3.3mm len=9.53mm, axis (0,0,-1), area 98.8mm2, adj f9,f42,f44,f46
  f42: plane 15.62x9.53mm, normal (-1,0,0), area 148.8mm2, adj f9,f41,f43,f46
  f43: cylinder r=3.3mm len=9.53mm, axis (0,0,-1), area 98.8mm2, adj f9,f42,f44,f46
  f44: plane 15.62x9.53mm, normal (1,0,0), area 148.8mm2, adj f9,f41,f43,f46
  f45: cylinder r=12.7mm len=25.4mm, axis (0,0,-1), area 380mm2, adj f9,f39,f40,f46
  f46: plane 36.58x25.4mm, normal (0,0,1), area 722.4mm2, adj f39,f40,f41,f42,f43,f44,f45,f59
  f47: plane 23.88x9.53mm, normal (-1,0,0), area 227.4mm2, adj f9,f53,f54,f56
  f48: plane 23.88x9.53mm, normal (1,0,0), area 227.4mm2, adj f9,f53,f54,f55
  f49: cylinder r=3.3mm len=9.53mm, axis (0,0,-1), area 98.8mm2, adj f9,f50,f52,f54
  f50: plane 15.62x9.53mm, normal (-1,0,0), area 148.8mm2, adj f9,f49,f51,f54
  f51: cylinder r=3.3mm len=9.53mm, axis (0,0,-1), area 98.8mm2, adj f9,f50,f52,f54
  f52: plane 15.62x9.53mm, normal (1,0,0), area 148.8mm2, adj f9,f49,f51,f54
  f53: cylinder r=12.7mm len=25.4mm, axis (0,0,-1), area 380mm2, adj f9,f47,f48,f54
  f54: plane 36.58x25.4mm, normal (0,0,1), area 722.4mm2, adj f47,f48,f49,f50,f51,f52,f53,f57
  f55: cylinder r=1.52mm len=11.05mm, axis (0,0,-1), area 24.1mm2, adj f0,f9,f48,f57
  f56: cylinder r=1.52mm len=11.05mm, axis (0,0,1), area 24.1mm2, adj f0,f9,f47,f57
  f57: cylinder r=1.52mm len=28.45mm, axis (1,0,0), area 63.5mm2, adj f0,f54,f55,f56
  f58: cylinder r=1.52mm len=11.05mm, axis (0,0,1), area 24.1mm2, adj f1,f9,f40,f59
  f59: cylinder r=1.52mm len=28.45mm, axis (-1,0,0), area 63.5mm2, adj f1,f46,f58,f60
  f60: cylinder r=1.52mm len=11.05mm, axis (0,0,-1), area 24.1mm2, adj f1,f9,f39,f59
PLACE A rot(axis=(1,0,0),148.3deg) t=(134.19,30.8,163.22)mm
PLACE B rot(axis=(0,0,-1),90deg) t=(-236.76,79.68,31.7)mm
PLACE C t=(134.19,-9.22,22.17)mm
PLACE D rot(axis=(0,0,1),144.8deg) t=(-236.76,-94.91,31.7)mm
PLACE E rot(axis=(-1,0,0),121.7deg) t=(105.61,-74.07,138.39)mm
PLACE F t=(17.24,-9.22,22.17)mm fixed
MATE pin_slot D.f1 <-> F.f43  axis (0,0,1) through (-236.76,-94.91,31.7)mm
MATE cylindrical A.f7 <-> F.f12  axis (-1,0,0) through (-73.71,-9.22,98.37)mm
MATE revolute C.f28 <-> A.f7  axis (1,0,0) through (-126.16,-9.22,98.37)mm
MATE fastened E.f5 <-> A.f4  axis (-1,0,0) through (143.71,-9.22,98.37)mm
MATE slider C.f28 <-> F.f12  axis (1,0,0) through (-81.71,-9.22,98.37)mm
MATE pin_slot F.f49 <-> B.f1  axis (0,0,1) through (-236.76,79.68,31.7)mm
